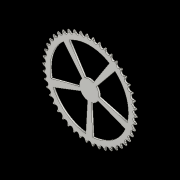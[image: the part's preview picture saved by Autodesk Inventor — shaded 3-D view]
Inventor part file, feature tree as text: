
AUTODESK INVENTOR PART (.ipt)
format: ipt  version: 2021 (Build 250183000, 183)  size: 963,072 bytes
history: native  units: mm
features: other x6, extrude x3, pattern_circular x2, pattern_linear x1, sketch x1
ambient origin geometry x8: Origin, YZ Plane, XZ Plane, XY Plane, X Axis, Y Axis, Z Axis, Center Point
bodies: Solid1 (feature_tree)
feature tree (13):
  other  "Theoretical Tooth Profile"
  other  "Tooth Profile"
  other  "Section Profile"
  other  "Shroud"
  other  "Strand"
  pattern_linear  "Strand Pattern"  Spacing1=1.36591mm  [1 undecoded]
  extrude  "Theoretical Tooth"  Depth=20.0mm
  extrude  "Tooth"  Depth=20.0mm
  pattern_circular  "Tooth Pattern"  [2 undecoded]
  other  "Timing Plane"
  extrude  "Extrusion4"  Depth=20.0mm
  pattern_circular  "Circular Pattern2"  [2 undecoded]
  sketch  "Sketch4"  dims[d0=186.101273mm d2=1.36591mm d3=3.91375mm d10=22.044267mm d11=2.929118mm d12=6.2mm d13=10.11375mm d14=10.85mm d18=10.0mm d19=0.0mm d20=460.0mm d21=360.0deg d23=3.81mm d28=0.0mm d29=0.0mm d30=3.069mm d31=166.745028mm d32=3.069mm d33=0.762mm d34=12.7mm d36=90.0deg d37=90.0deg d38=10.0mm d40=13.92mm d42=0.0mm d43=1.5345mm d44=24.093133mm d45=44.64mm d46=3.91375mm d47=10.0mm d48=0.0mm d49=0.0mm d50=10.0mm d51=80.0mm d52=21.118484mm d53=10.821041mm d54=20.0mm d55=20.245819mm d56=8.901179mm d57=0.0mm d58=0.0mm d59=50.0mm d60=360.0deg]
note: 5 required parameter values undecoded (feature->parameter linkage not recoverable at this tier; creation-order binding heuristic only, values carry confidence <= 0.55)
